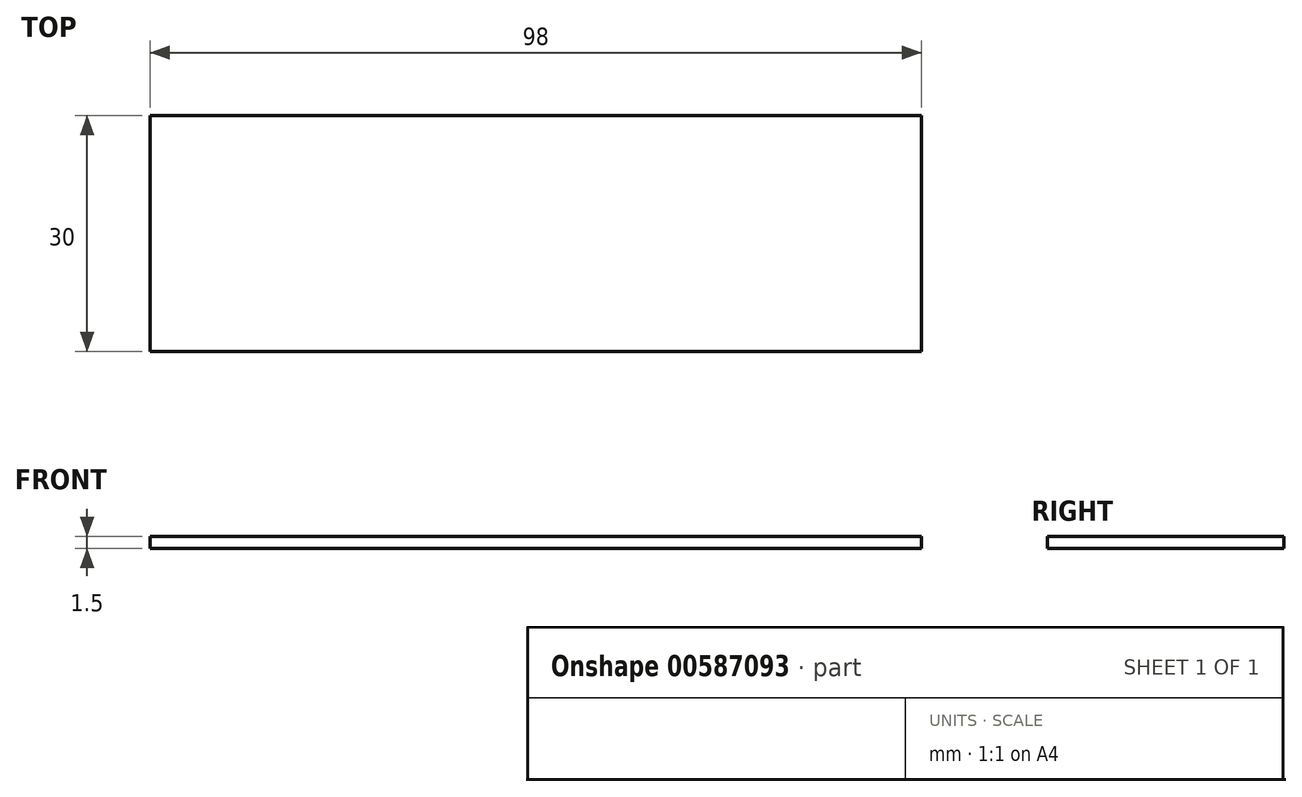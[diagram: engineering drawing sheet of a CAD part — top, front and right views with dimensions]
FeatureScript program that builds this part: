
annotation { "Feature Type Name" : "Feature", "Feature Type Description" : "" }
export const myFeature = defineFeature(function(context is Context, id is Id, definition is map)
    precondition{}
    {
        {
            var Q0;
            Q0=qCreatedBy(makeId("Top.planeOp"),FACE);
            var sketch = newSketch(context, id + "F0", { "sketchPlane" : qUnion([Q0])});
            skLineSegment(sketch, "E0.bottom", {"start": v(49, -15) * mm, "end": v(-49, -15) * mm});
            skLineSegment(sketch, "E0.top", {"start": v(49, 15) * mm, "end": v(-49, 15) * mm});
            skLineSegment(sketch, "E0.left", {"start": v(49, -15) * mm, "end": v(49, 15) * mm});
            skLineSegment(sketch, "E0.right", {"start": v(-49, -15) * mm, "end": v(-49, 15) * mm});
            skPoint(sketch, "E0.middle", {"position": v(0, 0) * mm});
            skSolve(sketch);
        }
        {
            var Q0;
            Q0 = qSketchRegion(id + "F0", true);
            extrude(context, id + "F1", {"entities" : qUnion([Q0]), "depth" : 1.5 * mm, "offsetDistance" : 25 * mm});
        }
    });
